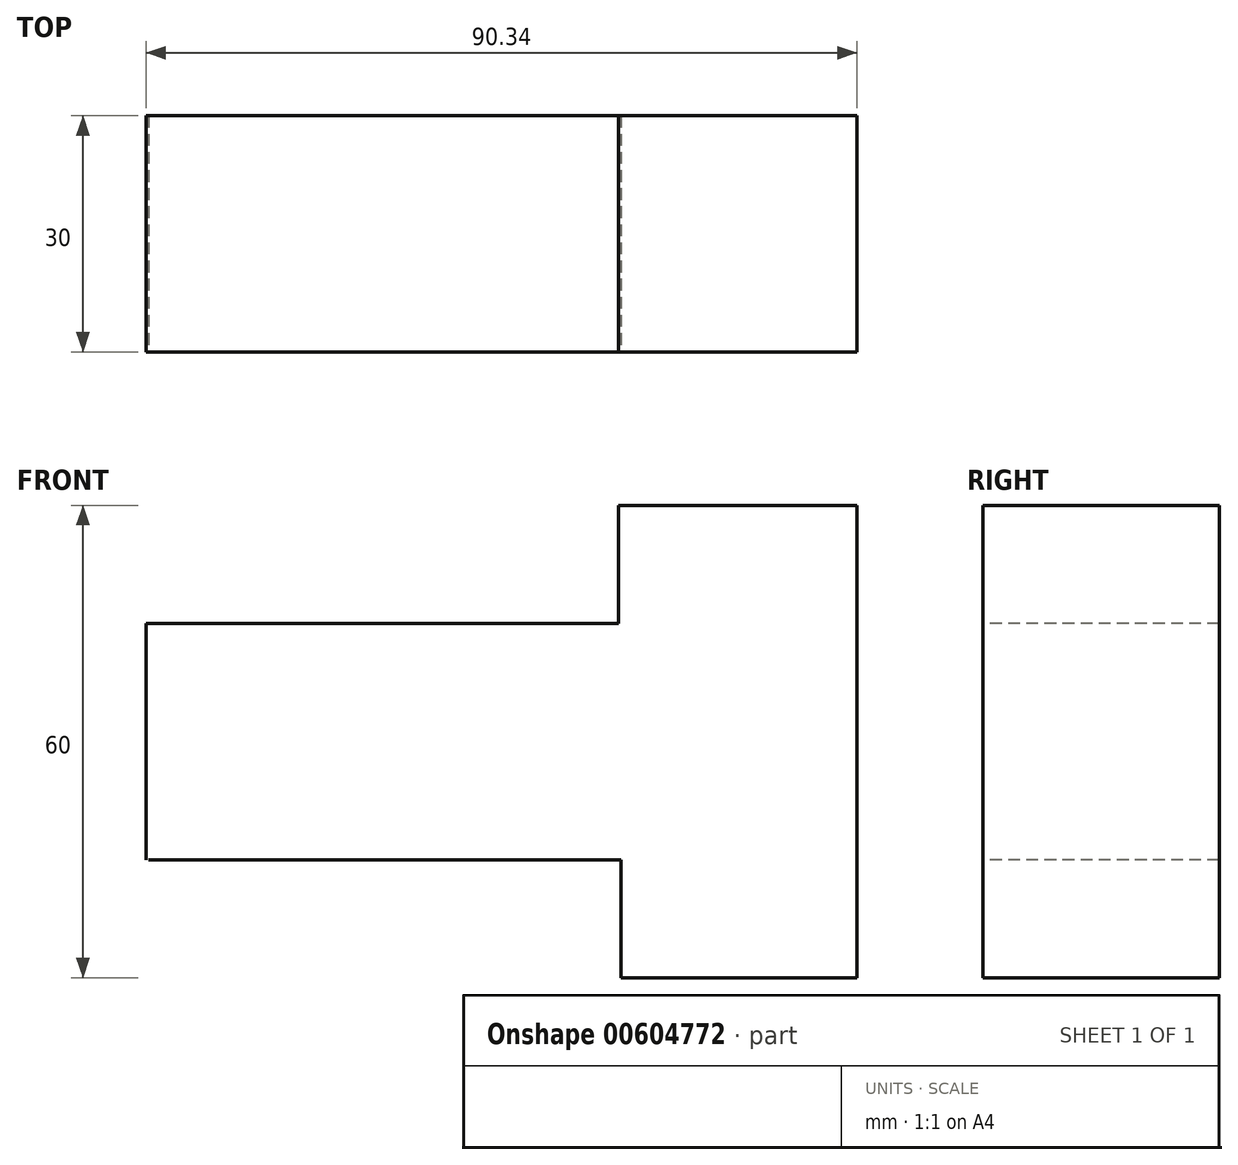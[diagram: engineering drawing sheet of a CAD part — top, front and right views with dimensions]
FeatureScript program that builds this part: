
annotation { "Feature Type Name" : "Feature", "Feature Type Description" : "" }
export const myFeature = defineFeature(function(context is Context, id is Id, definition is map)
    precondition{}
    {
        {
            var Q0;
            Q0=qCreatedBy(makeId("Front.planeOp"),FACE);
            var sketch = newSketch(context, id + "F0", { "sketchPlane" : qUnion([Q0])});
            skLineSegment(sketch, "E0", {"start": v(-36.75, 39.07) * mm, "end": v(-36.75, 9.07) * mm});
            skLineSegment(sketch, "E1", {"start": v(-36.4, 9.07) * mm, "end": v(23.6, 9.07) * mm});
            skLineSegment(sketch, "E2", {"start": v(23.6, 9.07) * mm, "end": v(23.6, -5.93) * mm});
            skLineSegment(sketch, "E3", {"start": v(23.6, -5.93) * mm, "end": v(53.6, -5.93) * mm});
            skLineSegment(sketch, "E4", {"start": v(53.6, -5.93) * mm, "end": v(53.6, 54.07) * mm});
            skLineSegment(sketch, "E5", {"start": v(53.6, 54.07) * mm, "end": v(23.25, 54.07) * mm});
            skLineSegment(sketch, "E6", {"start": v(-36.75, 39.07) * mm, "end": v(23.25, 39.07) * mm});
            skLineSegment(sketch, "E7", {"start": v(23.25, 39.07) * mm, "end": v(23.25, 54.07) * mm});
            skSolve(sketch);
        }
        {
            var Q0;
            Q0=sQuery(id+"F0.wireOp",EDGE,"E5");
            var Q1;
            Q1=sQuery(id+"F0.wireOp",EDGE,"E6");
            var Q2;
            Q2=sQuery(id+"F0.wireOp",EDGE,"E3");
            var Q3;
            Q3=sQuery(id+"F0.wireOp",EDGE,"E2");
            var Q4;
            Q4=sQuery(id+"F0.wireOp",EDGE,"E1");
            var Q5;
            Q5=sQuery(id+"F0.wireOp",EDGE,"E0");
            var Q6;
            Q6=sQuery(id+"F0.wireOp",EDGE,"E4");
            var Q7;
            Q7=sQuery(id+"F0.wireOp",EDGE,"E7");
            extrude(context, id + "F1", {"bodyType" : ToolBodyType.SURFACE, "surfaceEntities" : qUnion([Q0, Q1, Q2, Q3, Q4, Q5, Q6, Q7]), "depth" : 30 * mm, "offsetDistance" : 25.4 * mm});
        }
    });
